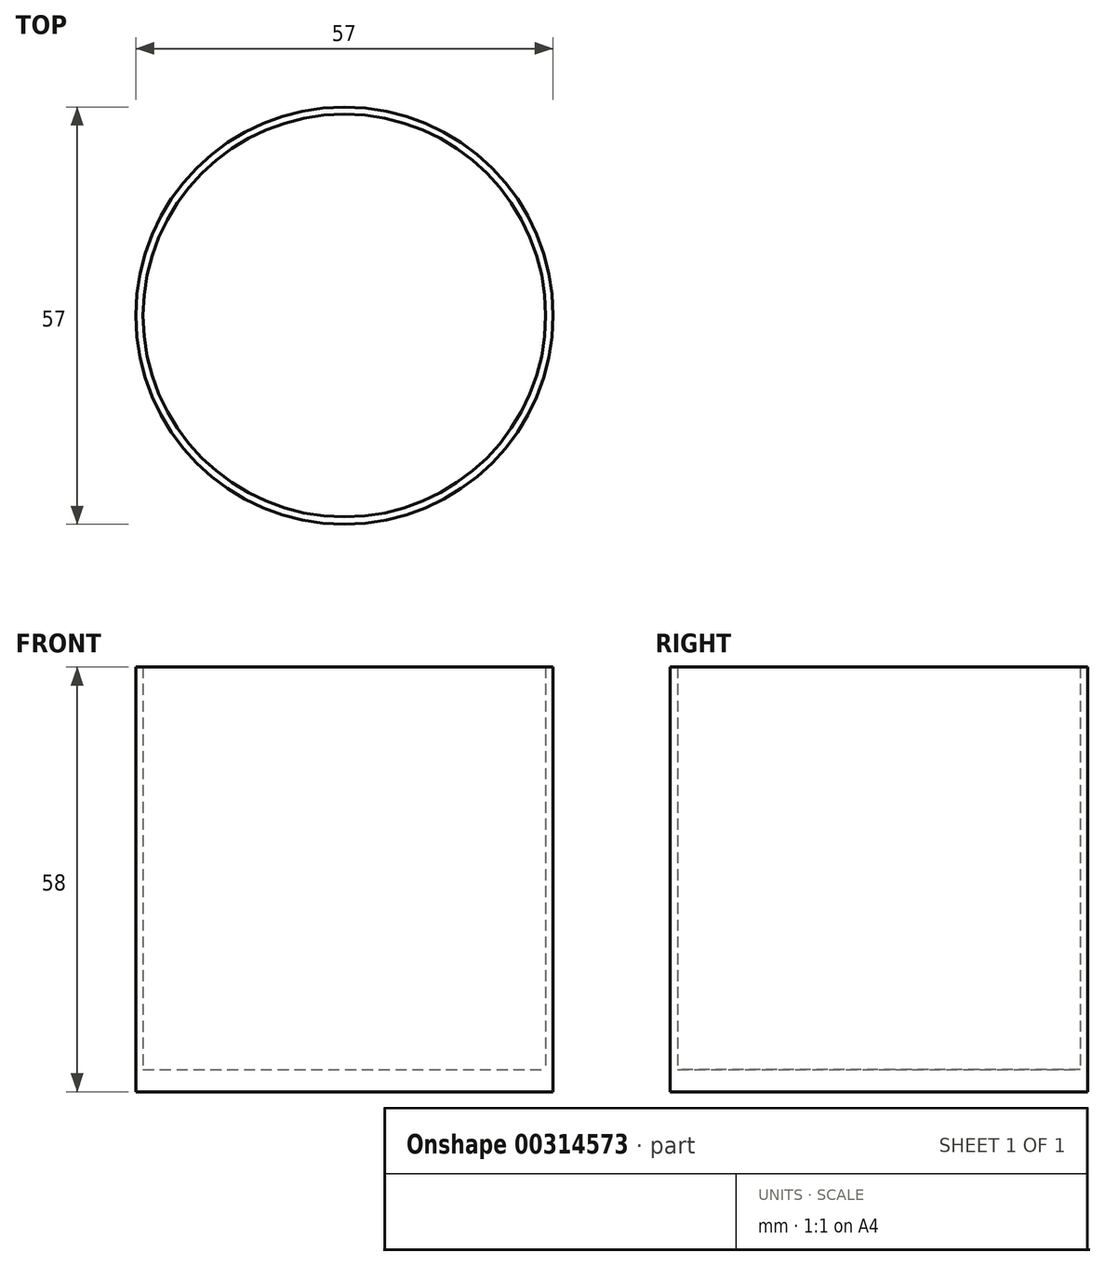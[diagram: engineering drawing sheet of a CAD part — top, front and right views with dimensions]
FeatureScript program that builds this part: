
annotation { "Feature Type Name" : "Feature", "Feature Type Description" : "" }
export const myFeature = defineFeature(function(context is Context, id is Id, definition is map)
    precondition{}
    {
        {
            var Q0;
            Q0=qCreatedBy(makeId("Top.planeOp"),FACE);
            var sketch = newSketch(context, id + "F0", { "sketchPlane" : qUnion([Q0])});
            skCircle(sketch, "E0", {"center": v(0, 0) * mm, "radius": 27.5 * mm});
            skSolve(sketch);
        }
        {
            var Q0;
            Q0=qCreatedBy(makeId("Top.planeOp"),FACE);
            var sketch = newSketch(context, id + "F1", { "sketchPlane" : qUnion([Q0])});
            skCircle(sketch, "E1", {"center": v(0, 0) * mm, "radius": 28.5 * mm});
            skSolve(sketch);
        }
        {
            var Q0;
            Q0=makeQuery(id+"F1.imprint","IMPRINT",FACE,{"disambiguationData":[TD([[makeQuery(id+"F1.imprint","IMPRINT",EDGE,{"derivedFrom":sQuery(id+"F1.wireOp",EDGE,"E1")}),1.0]])]});
            extrude(context, id + "F2", {"entities" : qUnion([Q0]), "depth" : 55 * mm});
        }
        {
            var Q0;
            Q0=sQuery(id+"F0.wireOp",VERTEX,"E0.center");
            var Q1;
            Q1=makeQuery(id+"F2.opExtrude","SWEPT_BODY",BODY,{"disambiguationData":[OSD([sQuery(id+"F1.wireOp",EDGE,"E1")])]});
            hole(context, id + "F3", {"style" : HoleStyle.SIMPLE, "endStyle" : HoleEndStyle.THROUGH, "oppositeDirection" : true, "holeDiameter" : 55 * mm, "tappedDepth" : 12.7 * mm, "tapClearance" : 3, "locations" : qUnion([Q0]), "scope" : qUnion([Q1])});
        }
        {
            var Q0;
            Q0=qCreatedBy(makeId("Top.planeOp"),FACE);
            cPlane(context, id + "F4", {"entities" : qUnion([Q0]), "cplaneType" : CPlaneType.OFFSET, "offset" : 3 * mm, "oppositeDirection" : true, "width" : 152.4 * mm, "height" : 152.4 * mm});
        }
        {
            var Q0;
            Q0=qCreatedBy(id+"F4.planeOp",FACE);
            var sketch = newSketch(context, id + "F5", { "sketchPlane" : qUnion([Q0])});
            skCircle(sketch, "E2", {"center": v(0, 0) * mm, "radius": 28.5 * mm});
            skSolve(sketch);
        }
        {
            var Q0;
            Q0 = qSketchRegion(id + "F5", true);
            extrude(context, id + "F6", {"entities" : qUnion([Q0]), "operationType" : NewBodyOperationType.ADD, "depth" : 3 * mm});
        }
    });
